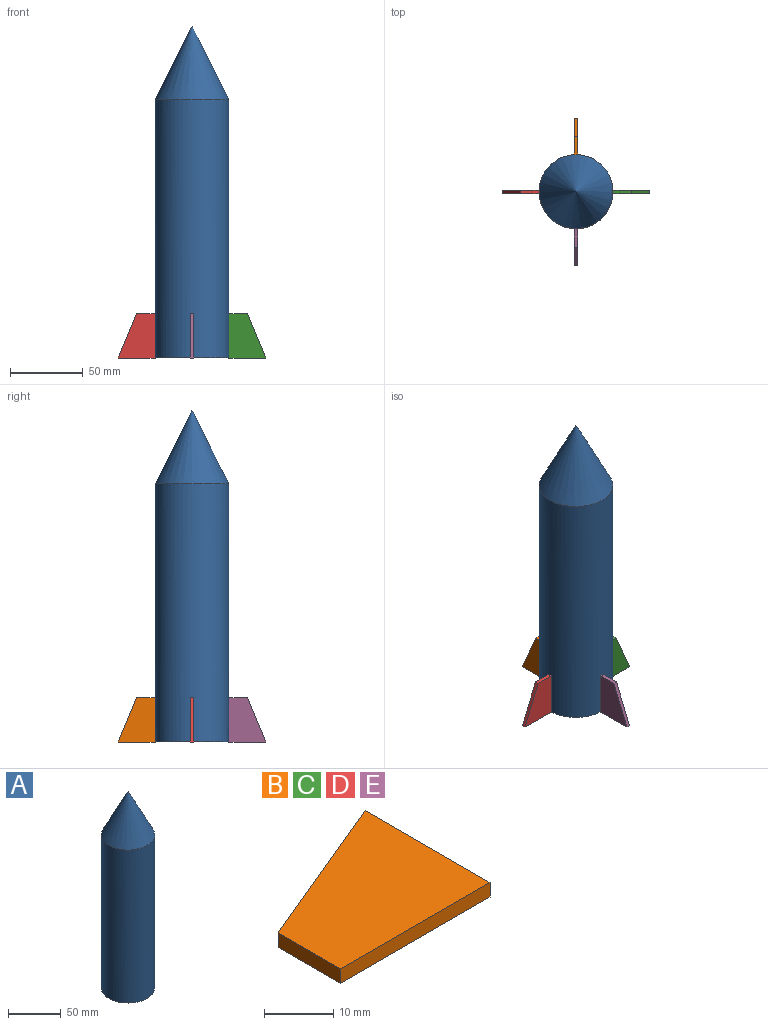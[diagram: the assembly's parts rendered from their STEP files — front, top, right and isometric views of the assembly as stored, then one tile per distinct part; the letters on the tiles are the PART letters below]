
ASSEMBLY  parts=5 mates=4
PART A: 5 faces, bbox 50.8x50.8x228.6 mm
  f0: cylinder r=10.79mm len=177.8mm, axis (0,0,-1), area 12059.6mm2, adj f2,f3
  f1: cylinder r=25.4mm len=177.8mm, axis (0,0,-1), area 28375.6mm2, adj f2,f4
  f2: plane 50.8x50.8mm, normal (0,0,-1), area 1660.7mm2, adj f0,f1
  f3: plane 21.59x21.59mm, normal (0,0,-1), area 366.1mm2, adj f0
  f4: cone r=25.4mm half-angle=26.6deg, axis (0,0,-1), area 4532.1mm2, adj f1
PART B: 6 faces, bbox 30.5x25.4x2.5 mm
  f0: plane 30.48x12.7mm, normal (-0.38,0.92,0), area 83.9mm2, adj f1,f3,f4,f5
  f1: plane 12.7x2.54mm, normal (-1,0,0), area 32.3mm2, adj f0,f2,f4,f5
  f2: plane 30.48x2.54mm, normal (0,-1,0), area 77.4mm2, adj f1,f3,f4,f5
  f3: plane 25.4x2.54mm, normal (1,0,0), area 64.5mm2, adj f0,f2,f4,f5
  f4: plane 30.48x25.4mm, normal (0,0,1), area 580.6mm2, adj f0,f1,f2,f3
  f5: plane 30.48x25.4mm, normal (0,0,-1), area 580.6mm2, adj f0,f1,f2,f3
PART C: same geometry as B
PART D: same geometry as B
PART E: same geometry as B
PLACE A t=(-69.07,53.52,4.25)mm
PLACE B rot(axis=(0,1,0),90deg) t=(-70.34,93.16,11.08)mm
PLACE C rot(axis=(0.58,0.58,-0.58),120deg) t=(-25.22,50.58,11.08)mm
PLACE D rot(axis=(-0.58,0.58,0.58),120deg) t=(-112.92,48.04,11.08)mm
PLACE E rot(axis=(-0.71,0,0.71),180deg) t=(-67.8,5.46,11.08)mm
MATE fastened D.f3 <-> A.f2  axis (0,0,-1) through (-107.17,49.31,4.25)mm
MATE fastened B.f3 <-> A.f2  axis (0,0,-1) through (-69.07,87.41,4.25)mm
MATE fastened E.f3 <-> A.f2  axis (0,0,-1) through (-69.07,11.21,4.25)mm
MATE fastened C.f3 <-> A.f2  axis (0,0,-1) through (-30.97,49.31,4.25)mm
